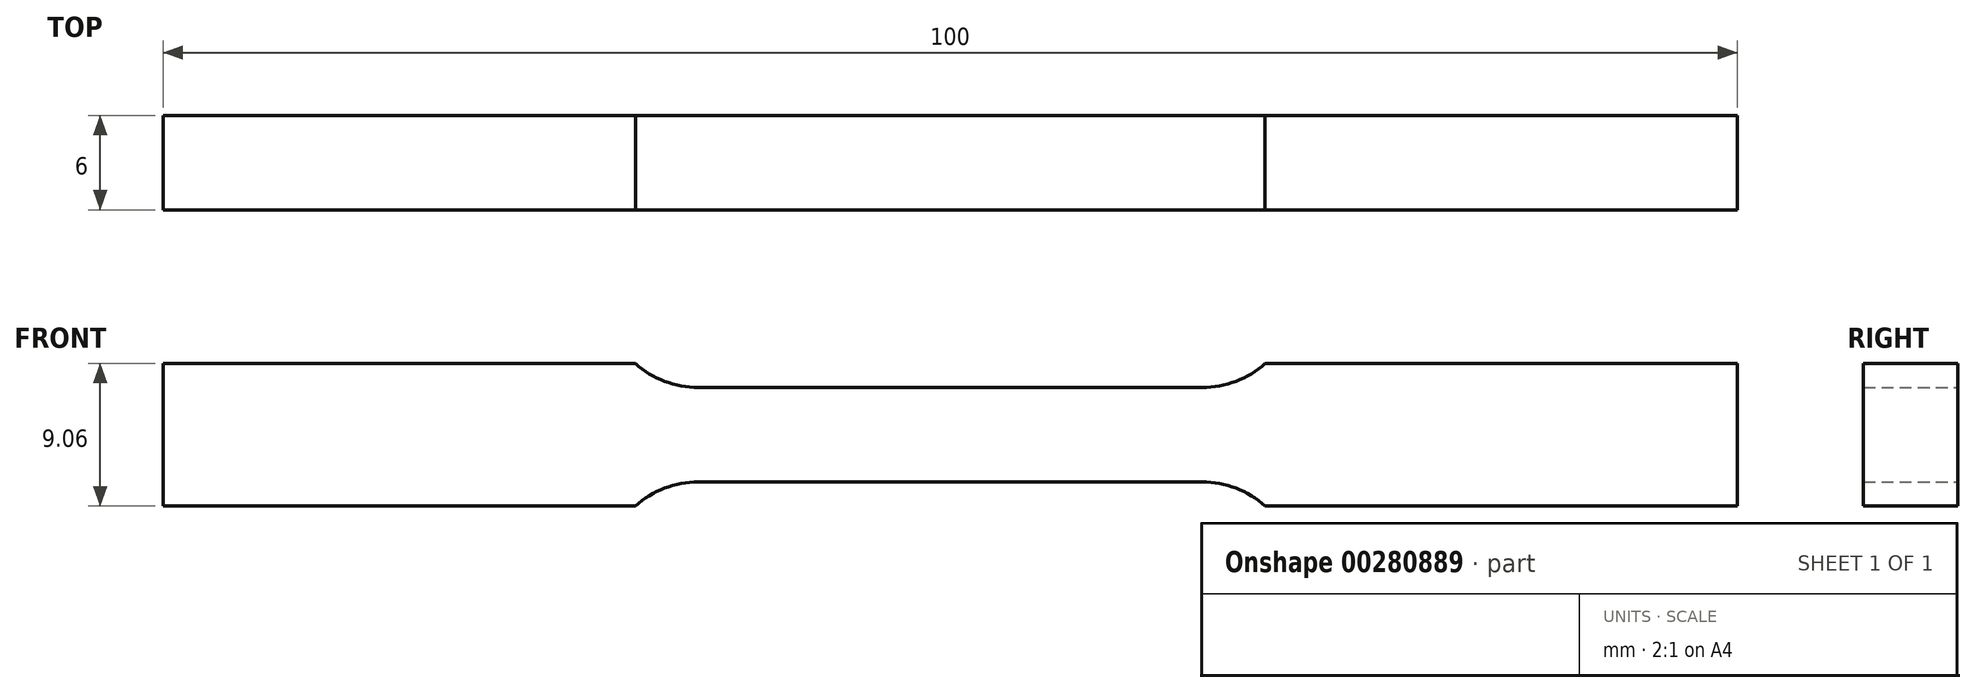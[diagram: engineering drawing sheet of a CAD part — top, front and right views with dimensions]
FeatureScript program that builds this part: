
annotation { "Feature Type Name" : "Feature", "Feature Type Description" : "" }
export const myFeature = defineFeature(function(context is Context, id is Id, definition is map)
    precondition{}
    {
        {
            var Q0;
            Q0=qCreatedBy(makeId("Front.planeOp"),FACE);
            var sketch = newSketch(context, id + "F0", { "sketchPlane" : qUnion([Q0])});
            skLineSegment(sketch, "E0", {"start": v(0, 3) * mm, "end": v(16, 3) * mm});
            skArc(sketch, "E1", {"start": v(16, 3) * mm, "mid": v(18.14, 3.4) * mm, "end": v(20, 4.53) * mm});
            skLineSegment(sketch, "E2", {"start": v(20, 4.53) * mm, "end": v(50, 4.53) * mm});
            skLineSegment(sketch, "E3", {"start": v(50, 4.53) * mm, "end": v(50, 0) * mm});
            skLineSegment(sketch, "E4.MirrorCS", {"start": v(0, -3) * mm, "end": v(16, -3) * mm});
            skLineSegment(sketch, "E5.MirrorCS", {"start": v(50, -4.53) * mm, "end": v(50, 0) * mm});
            skLineSegment(sketch, "E6.MirrorCS", {"start": v(20, -4.53) * mm, "end": v(50, -4.53) * mm});
            skArc(sketch, "E7.MirrorCS", {"start": v(16, -3) * mm, "mid": v(18.14, -3.4) * mm, "end": v(20, -4.53) * mm});
            skArc(sketch, "E8.MirrorCS", {"start": v(-16, -3) * mm, "mid": v(-18.14, -3.4) * mm, "end": v(-20, -4.53) * mm});
            skLineSegment(sketch, "E9.MirrorCS", {"start": v(-20, -4.53) * mm, "end": v(-50, -4.53) * mm});
            skArc(sketch, "E10.MirrorCS", {"start": v(-16, 3) * mm, "mid": v(-18.14, 3.4) * mm, "end": v(-20, 4.53) * mm});
            skLineSegment(sketch, "E11.MirrorCS", {"start": v(-20, 4.53) * mm, "end": v(-50, 4.53) * mm});
            skLineSegment(sketch, "E12.MirrorCS", {"start": v(-50, -4.53) * mm, "end": v(-50, 0) * mm});
            skLineSegment(sketch, "E13.MirrorCS", {"start": v(0, -3) * mm, "end": v(-16, -3) * mm});
            skLineSegment(sketch, "E14.MirrorCS", {"start": v(-50, 4.53) * mm, "end": v(-50, 0) * mm});
            skLineSegment(sketch, "E15.MirrorCS", {"start": v(0, 3) * mm, "end": v(-16, 3) * mm});
            skLineSegment(sketch, "E16.MirrorCS", {"start": v(0, 9) * mm, "end": v(16, 9) * mm});
            skSolve(sketch);
        }
        {
            var Q0;
            Q0 = qSketchRegion(id + "F0", true);
            extrude(context, id + "F1", {"entities" : qUnion([Q0]), "endBound" : BoundingType.SYMMETRIC, "depth" : 6 * mm});
        }
    });
